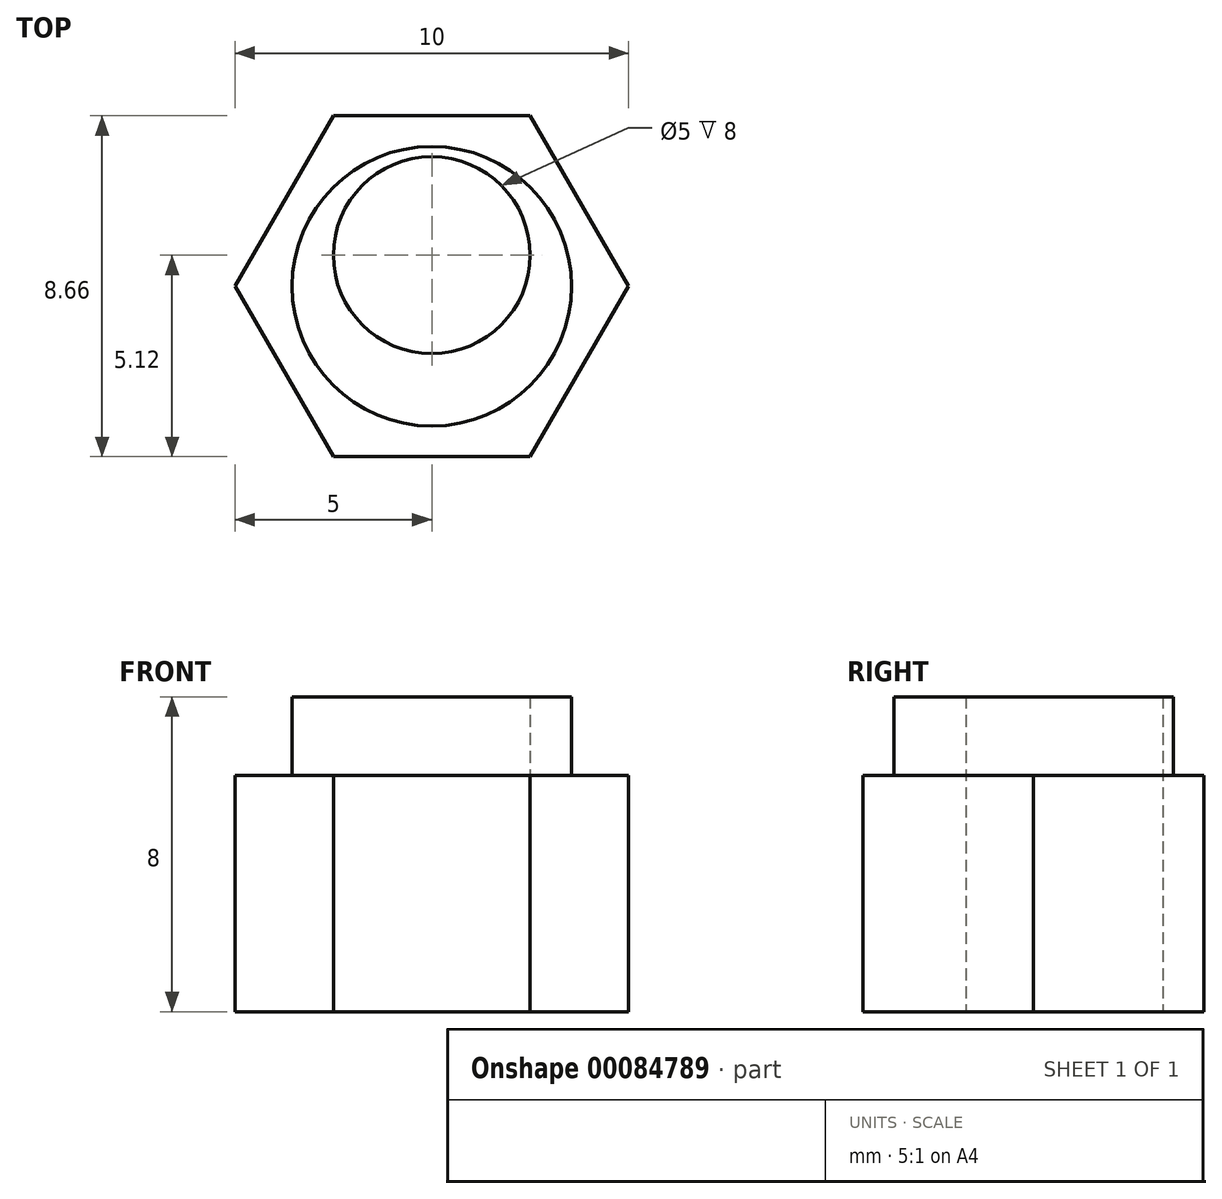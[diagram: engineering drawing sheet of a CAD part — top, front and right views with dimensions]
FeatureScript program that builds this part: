
annotation { "Feature Type Name" : "Feature", "Feature Type Description" : "" }
export const myFeature = defineFeature(function(context is Context, id is Id, definition is map)
    precondition{}
    {
        {
            var Q0;
            Q0=qCreatedBy(makeId("Top.planeOp"),FACE);
            var sketch = newSketch(context, id + "F0", { "sketchPlane" : qUnion([Q0])});
            skCircle(sketch, "E0.cCircle", {"center": v(0, 0) * mm, "radius": 5 * mm, "construction": true});
            skLineSegment(sketch, "E0.0", {"start": v(-2.5, 4.33) * mm, "end": v(2.5, 4.33) * mm});
            skLineSegment(sketch, "E0.1", {"start": v(2.5, 4.33) * mm, "end": v(5, 0) * mm});
            skLineSegment(sketch, "E0.2", {"start": v(5, 0) * mm, "end": v(2.5, -4.33) * mm});
            skLineSegment(sketch, "E0.3", {"start": v(2.5, -4.33) * mm, "end": v(-2.5, -4.33) * mm});
            skLineSegment(sketch, "E0.4", {"start": v(-2.5, -4.33) * mm, "end": v(-5, 0) * mm});
            skLineSegment(sketch, "E0.5", {"start": v(-5, 0) * mm, "end": v(-2.5, 4.33) * mm});
            skLineSegment(sketch, "E1", {"start": v(0, 0) * mm, "end": v(0, 0.79) * mm, "construction": true});
            skCircle(sketch, "E2", {"center": v(0, 0) * mm, "radius": 3.55 * mm});
            skCircle(sketch, "E3", {"center": v(0, 0.79) * mm, "radius": 2.5 * mm});
            skSolve(sketch);
        }
        {
            var Q0;
            Q0=makeQuery(id+"F0.imprint","IMPRINT",FACE,{"disambiguationData":[TD([[makeQuery(id+"F0.imprint","IMPRINT",EDGE,{"derivedFrom":sQuery(id+"F0.wireOp",EDGE,"E0.0")}),-1.0]])]});
            extrude(context, id + "F1", {"entities" : qUnion([Q0]), "depth" : 6 * mm});
        }
        {
            var Q0;
            Q0=makeQuery(id+"F0.imprint","IMPRINT",FACE,{"disambiguationData":[TD([[makeQuery(id+"F0.imprint","IMPRINT",EDGE,{"derivedFrom":sQuery(id+"F0.wireOp",EDGE,"E2")}),1.0]])]});
            extrude(context, id + "F2", {"entities" : qUnion([Q0]), "operationType" : NewBodyOperationType.ADD, "depth" : 8 * mm});
        }
    });
